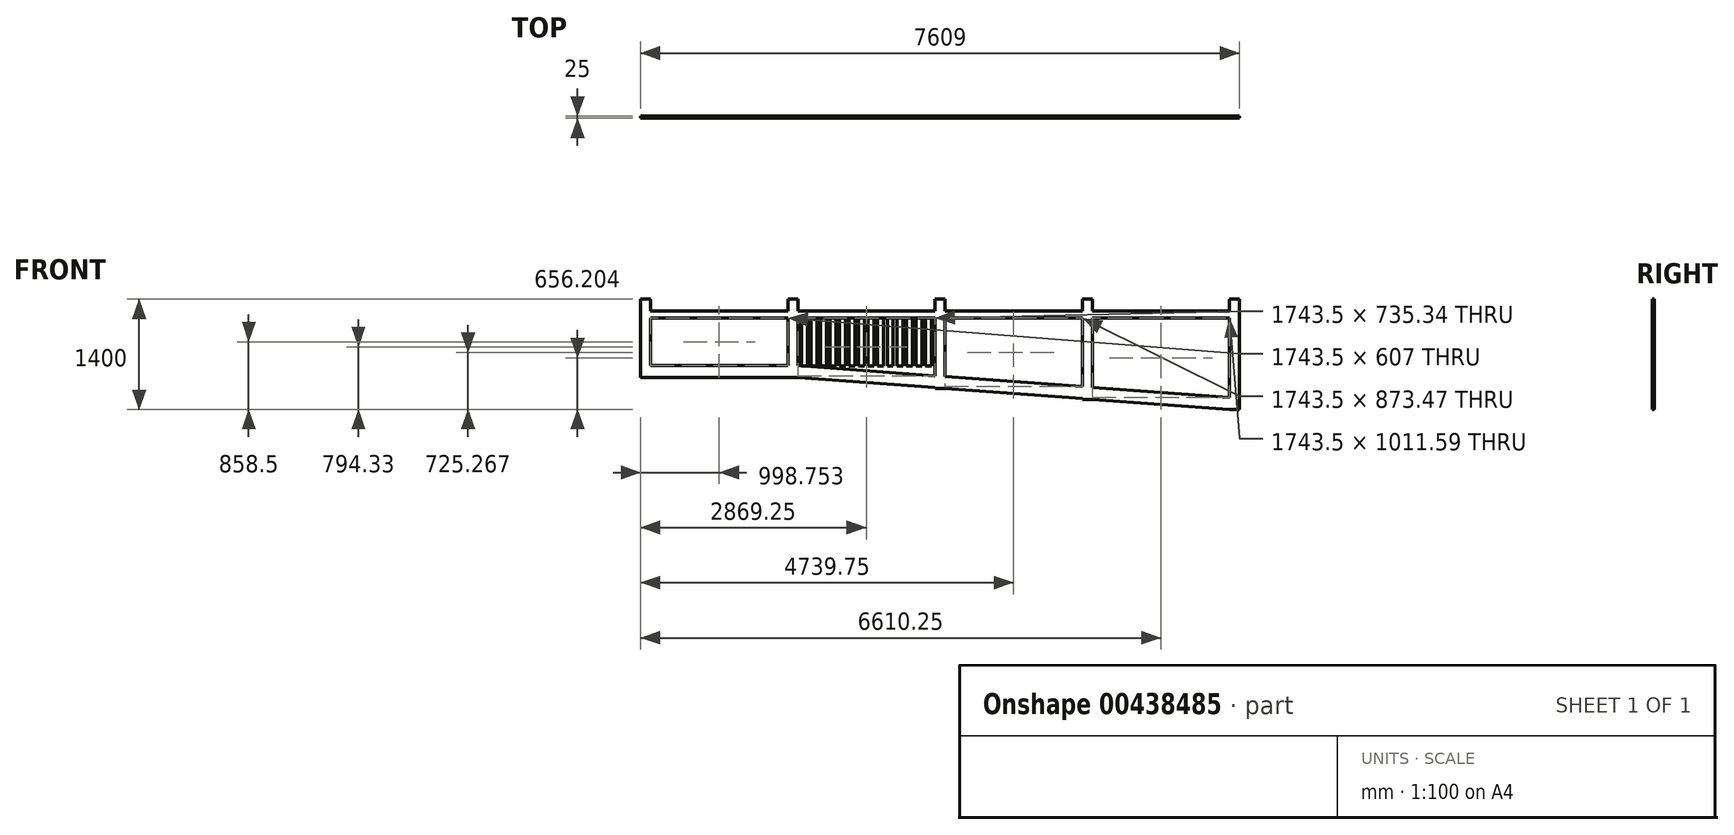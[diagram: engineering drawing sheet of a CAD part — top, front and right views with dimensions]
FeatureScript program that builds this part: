
annotation { "Feature Type Name" : "Feature", "Feature Type Description" : "" }
export const myFeature = defineFeature(function(context is Context, id is Id, definition is map)
    precondition{}
    {
        {
            var Q0;
            Q0=qCreatedBy(makeId("Front.planeOp"),FACE);
            var sketch = newSketch(context, id + "F0", { "sketchPlane" : qUnion([Q0])});
            skLineSegment(sketch, "E0", {"start": v(-3410.73, 0) * mm, "end": v(-1667.23, 0) * mm});
            skLineSegment(sketch, "E1", {"start": v(4071.27, 150) * mm, "end": v(4071.27, -1250) * mm});
            skLineSegment(sketch, "E2", {"start": v(-3410.73, -88) * mm, "end": v(-1667.23, -88) * mm});
            skLineSegment(sketch, "E3", {"start": v(-3537.73, 150) * mm, "end": v(-3537.73, -845) * mm});
            skLineSegment(sketch, "E4", {"start": v(-3537.73, 150) * mm, "end": v(-3410.73, 150) * mm});
            skLineSegment(sketch, "E5", {"start": v(-3410.73, 150) * mm, "end": v(-3410.73, 0) * mm});
            skLineSegment(sketch, "E6", {"start": v(-3410.73, -845) * mm, "end": v(-3537.73, -845) * mm});
            skLineSegment(sketch, "E7", {"start": v(4071.27, 150) * mm, "end": v(3944.27, 150) * mm});
            skLineSegment(sketch, "E8", {"start": v(3944.27, 150) * mm, "end": v(3944.27, -1250) * mm});
            skLineSegment(sketch, "E9", {"start": v(3944.27, -1250) * mm, "end": v(4071.27, -1250) * mm});
            skLineSegment(sketch, "E10", {"start": v(-1667.23, 150) * mm, "end": v(-1667.23, 0) * mm});
            skLineSegment(sketch, "E11", {"start": v(-1667.23, -845) * mm, "end": v(-1540.23, -845) * mm});
            skLineSegment(sketch, "E12", {"start": v(-1540.23, -845) * mm, "end": v(-1540.23, -88) * mm});
            skLineSegment(sketch, "E13", {"start": v(-1540.23, 150) * mm, "end": v(-1667.23, 150) * mm});
            skLineSegment(sketch, "E14", {"start": v(-3537.73, -845) * mm, "end": v(-1540.23, -845) * mm});
            skLineSegment(sketch, "E15", {"start": v(-3410.73, -695) * mm, "end": v(-1540.23, -695) * mm});
            skLineSegment(sketch, "E16", {"start": v(-1540.23, -845) * mm, "end": v(203.27, -973.75) * mm});
            skLineSegment(sketch, "E17", {"start": v(-1540.23, -694.6) * mm, "end": v(3944.27, -1099.6) * mm});
            skLineSegment(sketch, "E18", {"start": v(203.27, 150) * mm, "end": v(330.27, 150) * mm});
            skLineSegment(sketch, "E19", {"start": v(203.27, 150) * mm, "end": v(203.27, -973.75) * mm});
            skLineSegment(sketch, "E20", {"start": v(330.27, 150) * mm, "end": v(330.27, -983.13) * mm});
            skLineSegment(sketch, "E21", {"start": v(2073.77, 150) * mm, "end": v(2073.77, -1111.87) * mm});
            skLineSegment(sketch, "E22", {"start": v(2200.77, 150) * mm, "end": v(2200.77, -1121.25) * mm});
            skLineSegment(sketch, "E23.trimOffspring", {"start": v(2073.77, 150) * mm, "end": v(2200.77, 150) * mm});
            skLineSegment(sketch, "E24.trimOffspring", {"start": v(-1540.23, 0) * mm, "end": v(4071.27, 0) * mm});
            skLineSegment(sketch, "E25.trimOffspring", {"start": v(-1540.23, -88) * mm, "end": v(4071.27, -88) * mm});
            skLineSegment(sketch, "E26.trimOffspring", {"start": v(-1667.23, -88) * mm, "end": v(-1667.23, -695) * mm});
            skLineSegment(sketch, "E27.trimOffspring", {"start": v(-1540.23, 0) * mm, "end": v(-1540.23, 150) * mm});
            skLineSegment(sketch, "E28.trimOffspring", {"start": v(-3410.73, -88) * mm, "end": v(-3410.73, -695) * mm});
            skPoint(sketch, "E29.orphan", {"position": v(-3537.73, 0) * mm});
            skPoint(sketch, "E30.orphan", {"position": v(-3537.73, -88) * mm});
            skLineSegment(sketch, "E31", {"start": v(330.27, -983.13) * mm, "end": v(203.27, -983.13) * mm});
            skLineSegment(sketch, "E32", {"start": v(203.27, -983.13) * mm, "end": v(203.27, -973.75) * mm});
            skLineSegment(sketch, "E33.trimOffspring", {"start": v(330.27, -983.13) * mm, "end": v(2073.77, -1111.87) * mm});
            skLineSegment(sketch, "E34", {"start": v(2200.77, -1121.25) * mm, "end": v(2073.77, -1121.25) * mm});
            skLineSegment(sketch, "E35", {"start": v(2073.77, -1121.25) * mm, "end": v(2073.77, -1111.87) * mm});
            skLineSegment(sketch, "E36.trimOffspring", {"start": v(2200.77, -1121.25) * mm, "end": v(3944.27, -1250) * mm});
            skSolve(sketch);
        }
        {
            var Q0;
            {var subQ1=sQuery(id+"F0.wireOp",EDGE,"E12");var subQ7=makeQuery(id+"F0.imprint","IMPRINT",VERTEX,{"derivedFrom":subQ1});Q0=makeQuery(id+"F0.imprint","IMPRINT",FACE,{"disambiguationData":[TD([[makeQuery(id+"F0.imprint","IMPRINT",EDGE,{"disambiguationData":[TD([[subQ7,-1.0]])],"derivedFrom":subQ1}),-1.0]])]});}
            var Q1;
            Q1=makeQuery(id+"F0.imprint","IMPRINT",FACE,{"disambiguationData":[TD([[makeQuery(id+"F0.imprint","IMPRINT",EDGE,{"derivedFrom":sQuery(id+"F0.wireOp",EDGE,"E0")}),-1.0]])]});
            var Q2;
            {var subQ0=sQuery(id+"F0.wireOp",EDGE,"E19");var subQ1=sQuery(id+"F0.wireOp",EDGE,"E16");var subQ2=makeQuery(id+"F0.imprint","INTERSECT",VERTEX,{"derivedFrom":[subQ1,subQ0]});Q2=makeQuery(id+"F0.imprint","IMPRINT",FACE,{"disambiguationData":[TD([[makeQuery(id+"F0.imprint","IMPRINT",EDGE,{"disambiguationData":[TD([[subQ2,-1.0]])],"derivedFrom":subQ1}),1.0]])]});}
            var Q3;
            {var subQ0=sQuery(id+"F0.wireOp",EDGE,"E19");var subQ1=sQuery(id+"F0.wireOp",EDGE,"E17");var subQ2=makeQuery(id+"F0.imprint","INTERSECT",VERTEX,{"derivedFrom":[subQ1,subQ0]});Q3=makeQuery(id+"F0.imprint","IMPRINT",FACE,{"disambiguationData":[TD([[makeQuery(id+"F0.imprint","IMPRINT",EDGE,{"disambiguationData":[TD([[subQ2,-1.0]])],"derivedFrom":subQ1}),1.0]])]});}
            var Q4;
            {var subQ0=sQuery(id+"F0.wireOp",EDGE,"E18");Q4=makeQuery(id+"F0.imprint","IMPRINT",FACE,{"disambiguationData":[TD([[makeQuery(id+"F0.imprint","IMPRINT",EDGE,{"derivedFrom":subQ0}),-1.0]])]});}
            var Q5;
            {var subQ0=sQuery(id+"F0.wireOp",EDGE,"E24.trimOffspring");var subQ1=sQuery(id+"F0.wireOp",EDGE,"E19");var subQ2=makeQuery(id+"F0.imprint","INTERSECT",VERTEX,{"derivedFrom":[subQ1,subQ0]});Q5=makeQuery(id+"F0.imprint","IMPRINT",FACE,{"disambiguationData":[TD([[makeQuery(id+"F0.imprint","IMPRINT",EDGE,{"disambiguationData":[TD([[subQ2,-1.0]])],"derivedFrom":subQ1}),1.0]])]});}
            var Q6;
            {var subQ0=sQuery(id+"F0.wireOp",EDGE,"E24.trimOffspring");var subQ1=sQuery(id+"F0.wireOp",EDGE,"E20");var subQ2=makeQuery(id+"F0.imprint","INTERSECT",VERTEX,{"derivedFrom":[subQ1,subQ0]});Q6=makeQuery(id+"F0.imprint","IMPRINT",FACE,{"disambiguationData":[TD([[makeQuery(id+"F0.imprint","IMPRINT",EDGE,{"disambiguationData":[TD([[subQ2,-1.0]])],"derivedFrom":subQ1}),1.0]])]});}
            var Q7;
            {var subQ0=sQuery(id+"F0.wireOp",EDGE,"E20");var subQ1=sQuery(id+"F0.wireOp",EDGE,"E16");var subQ2=makeQuery(id+"F0.imprint","INTERSECT",VERTEX,{"derivedFrom":[subQ1,subQ0]});Q7=makeQuery(id+"F0.imprint","IMPRINT",FACE,{"disambiguationData":[TD([[makeQuery(id+"F0.imprint","IMPRINT",EDGE,{"disambiguationData":[TD([[subQ2,-1.0]])],"derivedFrom":subQ1}),1.0]])]});}
            var Q8;
            {var subQ0=sQuery(id+"F0.wireOp",EDGE,"E21");var subQ1=sQuery(id+"F0.wireOp",EDGE,"E17");var subQ2=makeQuery(id+"F0.imprint","INTERSECT",VERTEX,{"derivedFrom":[subQ1,subQ0]});Q8=makeQuery(id+"F0.imprint","IMPRINT",FACE,{"disambiguationData":[TD([[makeQuery(id+"F0.imprint","IMPRINT",EDGE,{"disambiguationData":[TD([[subQ2,-1.0]])],"derivedFrom":subQ1}),1.0]])]});}
            var Q9;
            {var subQ0=sQuery(id+"F0.wireOp",EDGE,"E21");var subQ1=sQuery(id+"F0.wireOp",EDGE,"E16");var subQ2=makeQuery(id+"F0.imprint","INTERSECT",VERTEX,{"derivedFrom":[subQ1,subQ0]});Q9=makeQuery(id+"F0.imprint","IMPRINT",FACE,{"disambiguationData":[TD([[makeQuery(id+"F0.imprint","IMPRINT",EDGE,{"disambiguationData":[TD([[subQ2,-1.0]])],"derivedFrom":subQ1}),1.0]])]});}
            var Q10;
            {var subQ0=sQuery(id+"F0.wireOp",EDGE,"E24.trimOffspring");var subQ1=sQuery(id+"F0.wireOp",EDGE,"E21");var subQ2=makeQuery(id+"F0.imprint","INTERSECT",VERTEX,{"derivedFrom":[subQ1,subQ0]});Q10=makeQuery(id+"F0.imprint","IMPRINT",FACE,{"disambiguationData":[TD([[makeQuery(id+"F0.imprint","IMPRINT",EDGE,{"disambiguationData":[TD([[subQ2,-1.0]])],"derivedFrom":subQ1}),1.0]])]});}
            var Q11;
            {var subQ0=sQuery(id+"F0.wireOp",EDGE,"E23.trimOffspring");Q11=makeQuery(id+"F0.imprint","IMPRINT",FACE,{"disambiguationData":[TD([[makeQuery(id+"F0.imprint","IMPRINT",EDGE,{"derivedFrom":subQ0}),-1.0]])]});}
            var Q12;
            {var subQ0=sQuery(id+"F0.wireOp",EDGE,"E24.trimOffspring");var subQ1=sQuery(id+"F0.wireOp",EDGE,"E8");var subQ2=makeQuery(id+"F0.imprint","INTERSECT",VERTEX,{"derivedFrom":[subQ1,subQ0]});Q12=makeQuery(id+"F0.imprint","IMPRINT",FACE,{"disambiguationData":[TD([[makeQuery(id+"F0.imprint","IMPRINT",EDGE,{"disambiguationData":[TD([[subQ2,-1.0]])],"derivedFrom":subQ1}),-1.0]])]});}
            var Q13;
            {var subQ0=sQuery(id+"F0.wireOp",EDGE,"E7");Q13=makeQuery(id+"F0.imprint","IMPRINT",FACE,{"disambiguationData":[TD([[makeQuery(id+"F0.imprint","IMPRINT",EDGE,{"derivedFrom":subQ0}),1.0]])]});}
            var Q14;
            {var subQ0=sQuery(id+"F0.wireOp",EDGE,"E24.trimOffspring");var subQ1=sQuery(id+"F0.wireOp",EDGE,"E1");var subQ2=makeQuery(id+"F0.imprint","INTERSECT",VERTEX,{"derivedFrom":[subQ1,subQ0]});Q14=makeQuery(id+"F0.imprint","IMPRINT",FACE,{"disambiguationData":[TD([[makeQuery(id+"F0.imprint","IMPRINT",EDGE,{"disambiguationData":[TD([[subQ2,-1.0]])],"derivedFrom":subQ1}),-1.0]])]});}
            var Q15;
            {var subQ0=sQuery(id+"F0.wireOp",EDGE,"E9");Q15=makeQuery(id+"F0.imprint","IMPRINT",FACE,{"disambiguationData":[TD([[makeQuery(id+"F0.imprint","IMPRINT",EDGE,{"derivedFrom":subQ0}),1.0]])]});}
            var Q16;
            {var subQ1=sQuery(id+"F0.wireOp",EDGE,"E8");var subQ3=sQuery(id+"F0.wireOp",EDGE,"E17");var subQ4=makeQuery(id+"F0.imprint","INTERSECT",VERTEX,{"derivedFrom":[subQ1,subQ3]});Q16=makeQuery(id+"F0.imprint","IMPRINT",FACE,{"disambiguationData":[TD([[makeQuery(id+"F0.imprint","IMPRINT",EDGE,{"disambiguationData":[TD([[subQ4,1.0]])],"derivedFrom":subQ3}),-1.0]])]});}
            var Q17;
            {var subQ5=sQuery(id+"F0.wireOp",EDGE,"E33.trimOffspring");Q17=makeQuery(id+"F0.imprint","IMPRINT",FACE,{"disambiguationData":[TD([[makeQuery(id+"F0.imprint","IMPRINT",EDGE,{"derivedFrom":subQ5}),1.0]])]});}
            var Q18;
            {var subQ0=sQuery(id+"F0.wireOp",EDGE,"E34");Q18=makeQuery(id+"F0.imprint","IMPRINT",FACE,{"disambiguationData":[TD([[makeQuery(id+"F0.imprint","IMPRINT",EDGE,{"derivedFrom":subQ0}),-1.0]])]});}
            var Q19;
            {var subQ0=sQuery(id+"F0.wireOp",EDGE,"E31");Q19=makeQuery(id+"F0.imprint","IMPRINT",FACE,{"disambiguationData":[TD([[makeQuery(id+"F0.imprint","IMPRINT",EDGE,{"derivedFrom":subQ0}),-1.0]])]});}
            extrude(context, id + "F1", {"entities" : qUnion([Q0, Q1, Q2, Q3, Q4, Q5, Q6, Q7, Q8, Q9, Q10, Q11, Q12, Q13, Q14, Q15, Q16, Q17, Q18, Q19]), "depth" : 25 * mm});
        }
        {
            var Q0;
            Q0=makeQuery(id+"F1.opExtrude","CAP_FACE",FACE,{"disambiguationData":[OSD([sQuery(id+"F0.wireOp",EDGE,"E0"),sQuery(id+"F0.wireOp",EDGE,"E1"),sQuery(id+"F0.wireOp",EDGE,"E2"),sQuery(id+"F0.wireOp",EDGE,"E3"),sQuery(id+"F0.wireOp",EDGE,"E4"),sQuery(id+"F0.wireOp",EDGE,"E5"),sQuery(id+"F0.wireOp",EDGE,"E7"),sQuery(id+"F0.wireOp",EDGE,"E8"),sQuery(id+"F0.wireOp",EDGE,"E9"),sQuery(id+"F0.wireOp",EDGE,"E10"),sQuery(id+"F0.wireOp",EDGE,"E12"),sQuery(id+"F0.wireOp",EDGE,"E13"),sQuery(id+"F0.wireOp",EDGE,"E14"),sQuery(id+"F0.wireOp",EDGE,"E15"),sQuery(id+"F0.wireOp",EDGE,"E16"),sQuery(id+"F0.wireOp",EDGE,"E17"),sQuery(id+"F0.wireOp",EDGE,"E18"),sQuery(id+"F0.wireOp",EDGE,"E19"),sQuery(id+"F0.wireOp",EDGE,"E20"),sQuery(id+"F0.wireOp",EDGE,"E21"),sQuery(id+"F0.wireOp",EDGE,"E22"),sQuery(id+"F0.wireOp",EDGE,"E23.trimOffspring"),sQuery(id+"F0.wireOp",EDGE,"E24.trimOffspring"),sQuery(id+"F0.wireOp",EDGE,"E25.trimOffspring"),sQuery(id+"F0.wireOp",EDGE,"E26.trimOffspring"),sQuery(id+"F0.wireOp",EDGE,"E27.trimOffspring"),sQuery(id+"F0.wireOp",EDGE,"E28.trimOffspring"),sQuery(id+"F0.wireOp",EDGE,"E31"),sQuery(id+"F0.wireOp",EDGE,"E32"),sQuery(id+"F0.wireOp",EDGE,"E33.trimOffspring"),sQuery(id+"F0.wireOp",EDGE,"E34"),sQuery(id+"F0.wireOp",EDGE,"E35"),sQuery(id+"F0.wireOp",EDGE,"E36.trimOffspring")])],"isStart":false});
            var sketch = newSketch(context, id + "F2", { "sketchPlane" : qUnion([Q0])});
            skLineSegment(sketch, "E37", {"start": v(-1494.97, -697.93) * mm, "end": v(-1494.97, 395.8) * mm});
            skLineSegment(sketch, "E38", {"start": v(-1494.97, 395.8) * mm, "end": v(-1418.97, 395.8) * mm});
            skLineSegment(sketch, "E39", {"start": v(-1418.97, 395.8) * mm, "end": v(-1418.97, -697.93) * mm});
            skLineSegment(sketch, "E40", {"start": v(-1418.97, -697.93) * mm, "end": v(-1494.97, -697.93) * mm});
            skLineSegment(sketch, "E41.1.0.0", {"start": v(-1297.7, 395.8) * mm, "end": v(-1297.7, -697.93) * mm});
            skLineSegment(sketch, "E41.1.0.1", {"start": v(-1297.7, -697.93) * mm, "end": v(-1373.7, -697.93) * mm});
            skLineSegment(sketch, "E41.1.0.2", {"start": v(-1373.7, -697.93) * mm, "end": v(-1373.7, 395.8) * mm});
            skLineSegment(sketch, "E41.1.0.3", {"start": v(-1373.7, 395.8) * mm, "end": v(-1297.7, 395.8) * mm});
            skLineSegment(sketch, "E41.2.0.0", {"start": v(-1176.44, 395.8) * mm, "end": v(-1176.44, -697.93) * mm});
            skLineSegment(sketch, "E41.2.0.1", {"start": v(-1176.44, -697.93) * mm, "end": v(-1252.44, -697.93) * mm});
            skLineSegment(sketch, "E41.2.0.2", {"start": v(-1252.44, -697.93) * mm, "end": v(-1252.44, 395.8) * mm});
            skLineSegment(sketch, "E41.2.0.3", {"start": v(-1252.44, 395.8) * mm, "end": v(-1176.44, 395.8) * mm});
            skLineSegment(sketch, "E41.3.0.0", {"start": v(-1055.17, 395.8) * mm, "end": v(-1055.17, -697.93) * mm});
            skLineSegment(sketch, "E41.3.0.1", {"start": v(-1055.17, -697.93) * mm, "end": v(-1131.17, -697.93) * mm});
            skLineSegment(sketch, "E41.3.0.2", {"start": v(-1131.17, -697.93) * mm, "end": v(-1131.17, 395.8) * mm});
            skLineSegment(sketch, "E41.3.0.3", {"start": v(-1131.17, 395.8) * mm, "end": v(-1055.17, 395.8) * mm});
            skLineSegment(sketch, "E41.4.0.0", {"start": v(-933.9, 395.8) * mm, "end": v(-933.9, -697.93) * mm});
            skLineSegment(sketch, "E41.4.0.1", {"start": v(-933.9, -697.93) * mm, "end": v(-1009.9, -697.93) * mm});
            skLineSegment(sketch, "E41.4.0.2", {"start": v(-1009.9, -697.93) * mm, "end": v(-1009.9, 395.8) * mm});
            skLineSegment(sketch, "E41.4.0.3", {"start": v(-1009.9, 395.8) * mm, "end": v(-933.9, 395.8) * mm});
            skLineSegment(sketch, "E41.5.0.0", {"start": v(-812.64, 395.8) * mm, "end": v(-812.64, -697.93) * mm});
            skLineSegment(sketch, "E41.5.0.1", {"start": v(-812.64, -697.93) * mm, "end": v(-888.64, -697.93) * mm});
            skLineSegment(sketch, "E41.5.0.2", {"start": v(-888.64, -697.93) * mm, "end": v(-888.64, 395.8) * mm});
            skLineSegment(sketch, "E41.5.0.3", {"start": v(-888.64, 395.8) * mm, "end": v(-812.64, 395.8) * mm});
            skLineSegment(sketch, "E41.6.0.0", {"start": v(-691.37, 395.8) * mm, "end": v(-691.37, -697.93) * mm});
            skLineSegment(sketch, "E41.6.0.1", {"start": v(-691.37, -697.93) * mm, "end": v(-767.37, -697.93) * mm});
            skLineSegment(sketch, "E41.6.0.2", {"start": v(-767.37, -697.93) * mm, "end": v(-767.37, 395.8) * mm});
            skLineSegment(sketch, "E41.6.0.3", {"start": v(-767.37, 395.8) * mm, "end": v(-691.37, 395.8) * mm});
            skLineSegment(sketch, "E41.7.0.0", {"start": v(-570.1, 395.8) * mm, "end": v(-570.1, -697.93) * mm});
            skLineSegment(sketch, "E41.7.0.1", {"start": v(-570.1, -697.93) * mm, "end": v(-646.1, -697.93) * mm});
            skLineSegment(sketch, "E41.7.0.2", {"start": v(-646.1, -697.93) * mm, "end": v(-646.1, 395.8) * mm});
            skLineSegment(sketch, "E41.7.0.3", {"start": v(-646.1, 395.8) * mm, "end": v(-570.1, 395.8) * mm});
            skLineSegment(sketch, "E41.8.0.0", {"start": v(-448.84, 395.8) * mm, "end": v(-448.84, -697.93) * mm});
            skLineSegment(sketch, "E41.8.0.1", {"start": v(-448.84, -697.93) * mm, "end": v(-524.84, -697.93) * mm});
            skLineSegment(sketch, "E41.8.0.2", {"start": v(-524.84, -697.93) * mm, "end": v(-524.84, 395.8) * mm});
            skLineSegment(sketch, "E41.8.0.3", {"start": v(-524.84, 395.8) * mm, "end": v(-448.84, 395.8) * mm});
            skLineSegment(sketch, "E41.9.0.0", {"start": v(-327.57, 395.8) * mm, "end": v(-327.57, -697.93) * mm});
            skLineSegment(sketch, "E41.9.0.1", {"start": v(-327.57, -697.93) * mm, "end": v(-403.57, -697.93) * mm});
            skLineSegment(sketch, "E41.9.0.2", {"start": v(-403.57, -697.93) * mm, "end": v(-403.57, 395.8) * mm});
            skLineSegment(sketch, "E41.9.0.3", {"start": v(-403.57, 395.8) * mm, "end": v(-327.57, 395.8) * mm});
            skLineSegment(sketch, "E41.10.0.0", {"start": v(-206.3, 395.8) * mm, "end": v(-206.3, -697.93) * mm});
            skLineSegment(sketch, "E41.10.0.1", {"start": v(-206.3, -697.93) * mm, "end": v(-282.3, -697.93) * mm});
            skLineSegment(sketch, "E41.10.0.2", {"start": v(-282.3, -697.93) * mm, "end": v(-282.3, 395.8) * mm});
            skLineSegment(sketch, "E41.10.0.3", {"start": v(-282.3, 395.8) * mm, "end": v(-206.3, 395.8) * mm});
            skLineSegment(sketch, "E41.11.0.0", {"start": v(-85.04, 395.8) * mm, "end": v(-85.04, -697.93) * mm});
            skLineSegment(sketch, "E41.11.0.1", {"start": v(-85.04, -697.93) * mm, "end": v(-161.04, -697.93) * mm});
            skLineSegment(sketch, "E41.11.0.2", {"start": v(-161.04, -697.93) * mm, "end": v(-161.04, 395.8) * mm});
            skLineSegment(sketch, "E41.11.0.3", {"start": v(-161.04, 395.8) * mm, "end": v(-85.04, 395.8) * mm});
            skLineSegment(sketch, "E41.12.0.0", {"start": v(36.22, 395.8) * mm, "end": v(36.22, -697.93) * mm});
            skLineSegment(sketch, "E41.12.0.1", {"start": v(36.22, -697.93) * mm, "end": v(-39.78, -697.93) * mm});
            skLineSegment(sketch, "E41.12.0.2", {"start": v(-39.78, -697.93) * mm, "end": v(-39.78, 395.8) * mm});
            skLineSegment(sketch, "E41.12.0.3", {"start": v(-39.78, 395.8) * mm, "end": v(36.22, 395.8) * mm});
            skLineSegment(sketch, "E41.13.0.0", {"start": v(157.5, 395.8) * mm, "end": v(157.5, -697.93) * mm});
            skLineSegment(sketch, "E41.13.0.1", {"start": v(157.5, -697.93) * mm, "end": v(81.5, -697.93) * mm});
            skLineSegment(sketch, "E41.13.0.2", {"start": v(81.5, -697.93) * mm, "end": v(81.5, 395.8) * mm});
            skLineSegment(sketch, "E41.13.0.3", {"start": v(81.5, 395.8) * mm, "end": v(157.5, 395.8) * mm});
            skLineSegment(sketch, "E42", {"start": v(119.5, -697.93) * mm, "end": v(119.5, -817.15) * mm});
            skLineSegment(sketch, "E43", {"start": v(-1.78, -697.93) * mm, "end": v(-1.78, -808.2) * mm});
            skLineSegment(sketch, "E44", {"start": v(-123.04, -697.93) * mm, "end": v(-123.04, -799.24) * mm});
            skLineSegment(sketch, "E45", {"start": v(-244.3, -697.93) * mm, "end": v(-244.3, -790.29) * mm});
            skLineSegment(sketch, "E46", {"start": v(-365.57, -697.93) * mm, "end": v(-365.57, -781.33) * mm});
            skLineSegment(sketch, "E47", {"start": v(-486.84, -697.93) * mm, "end": v(-486.84, -772.38) * mm});
            skLineSegment(sketch, "E48", {"start": v(-608.1, -697.93) * mm, "end": v(-608.1, -763.42) * mm});
            skLineSegment(sketch, "E49", {"start": v(-729.37, -697.93) * mm, "end": v(-729.37, -754.47) * mm});
            skLineSegment(sketch, "E50", {"start": v(-850.64, -697.93) * mm, "end": v(-850.64, -745.51) * mm});
            skLineSegment(sketch, "E51", {"start": v(-971.9, -697.93) * mm, "end": v(-971.9, -736.56) * mm});
            skLineSegment(sketch, "E52", {"start": v(-1093.17, -697.93) * mm, "end": v(-1093.17, -727.6) * mm});
            skLineSegment(sketch, "E53", {"start": v(-1214.44, -697.93) * mm, "end": v(-1214.44, -718.65) * mm});
            skLineSegment(sketch, "E54", {"start": v(-1335.7, -697.93) * mm, "end": v(-1335.7, -709.7) * mm});
            skLineSegment(sketch, "E55", {"start": v(-1456.97, -697.93) * mm, "end": v(-1456.97, -700.74) * mm});
            skSolve(sketch);
        }
        {
            var Q0;
            {var subQ0=sQuery(id+"F2.wireOp",EDGE,"E40");Q0=makeQuery(id+"F2.imprint","IMPRINT",FACE,{"disambiguationData":[TD([[makeQuery(id+"F2.imprint","IMPRINT",EDGE,{"derivedFrom":subQ0}),-1.0]])]});}
            var Q1;
            {var subQ0=sQuery(id+"F2.wireOp",EDGE,"E41.1.0.1");Q1=makeQuery(id+"F2.imprint","IMPRINT",FACE,{"disambiguationData":[TD([[makeQuery(id+"F2.imprint","IMPRINT",EDGE,{"derivedFrom":subQ0}),-1.0]])]});}
            var Q2;
            {var subQ0=sQuery(id+"F2.wireOp",EDGE,"E41.2.0.1");Q2=makeQuery(id+"F2.imprint","IMPRINT",FACE,{"disambiguationData":[TD([[makeQuery(id+"F2.imprint","IMPRINT",EDGE,{"derivedFrom":subQ0}),-1.0]])]});}
            var Q3;
            {var subQ0=sQuery(id+"F2.wireOp",EDGE,"E41.3.0.1");Q3=makeQuery(id+"F2.imprint","IMPRINT",FACE,{"disambiguationData":[TD([[makeQuery(id+"F2.imprint","IMPRINT",EDGE,{"derivedFrom":subQ0}),-1.0]])]});}
            var Q4;
            {var subQ0=sQuery(id+"F2.wireOp",EDGE,"E41.4.0.1");Q4=makeQuery(id+"F2.imprint","IMPRINT",FACE,{"disambiguationData":[TD([[makeQuery(id+"F2.imprint","IMPRINT",EDGE,{"derivedFrom":subQ0}),-1.0]])]});}
            var Q5;
            {var subQ0=sQuery(id+"F2.wireOp",EDGE,"E41.5.0.1");Q5=makeQuery(id+"F2.imprint","IMPRINT",FACE,{"disambiguationData":[TD([[makeQuery(id+"F2.imprint","IMPRINT",EDGE,{"derivedFrom":subQ0}),-1.0]])]});}
            var Q6;
            {var subQ0=sQuery(id+"F2.wireOp",EDGE,"E41.6.0.1");Q6=makeQuery(id+"F2.imprint","IMPRINT",FACE,{"disambiguationData":[TD([[makeQuery(id+"F2.imprint","IMPRINT",EDGE,{"derivedFrom":subQ0}),-1.0]])]});}
            var Q7;
            {var subQ0=sQuery(id+"F2.wireOp",EDGE,"E41.7.0.1");Q7=makeQuery(id+"F2.imprint","IMPRINT",FACE,{"disambiguationData":[TD([[makeQuery(id+"F2.imprint","IMPRINT",EDGE,{"derivedFrom":subQ0}),-1.0]])]});}
            var Q8;
            {var subQ0=sQuery(id+"F2.wireOp",EDGE,"E41.8.0.1");Q8=makeQuery(id+"F2.imprint","IMPRINT",FACE,{"disambiguationData":[TD([[makeQuery(id+"F2.imprint","IMPRINT",EDGE,{"derivedFrom":subQ0}),-1.0]])]});}
            var Q9;
            {var subQ0=sQuery(id+"F2.wireOp",EDGE,"E41.9.0.1");Q9=makeQuery(id+"F2.imprint","IMPRINT",FACE,{"disambiguationData":[TD([[makeQuery(id+"F2.imprint","IMPRINT",EDGE,{"derivedFrom":subQ0}),-1.0]])]});}
            var Q10;
            {var subQ0=sQuery(id+"F2.wireOp",EDGE,"E41.10.0.1");Q10=makeQuery(id+"F2.imprint","IMPRINT",FACE,{"disambiguationData":[TD([[makeQuery(id+"F2.imprint","IMPRINT",EDGE,{"derivedFrom":subQ0}),-1.0]])]});}
            var Q11;
            {var subQ0=sQuery(id+"F2.wireOp",EDGE,"E41.11.0.1");Q11=makeQuery(id+"F2.imprint","IMPRINT",FACE,{"disambiguationData":[TD([[makeQuery(id+"F2.imprint","IMPRINT",EDGE,{"derivedFrom":subQ0}),-1.0]])]});}
            var Q12;
            {var subQ0=sQuery(id+"F2.wireOp",EDGE,"E41.12.0.1");Q12=makeQuery(id+"F2.imprint","IMPRINT",FACE,{"disambiguationData":[TD([[makeQuery(id+"F2.imprint","IMPRINT",EDGE,{"derivedFrom":subQ0}),-1.0]])]});}
            var Q13;
            {var subQ0=sQuery(id+"F2.wireOp",EDGE,"E41.13.0.1");Q13=makeQuery(id+"F2.imprint","IMPRINT",FACE,{"disambiguationData":[TD([[makeQuery(id+"F2.imprint","IMPRINT",EDGE,{"derivedFrom":subQ0}),-1.0]])]});}
            extrude(context, id + "F3", {"entities" : qUnion([Q0, Q1, Q2, Q3, Q4, Q5, Q6, Q7, Q8, Q9, Q10, Q11, Q12, Q13]), "oppositeDirection" : true, "depth" : 25 * mm});
        }
    });
